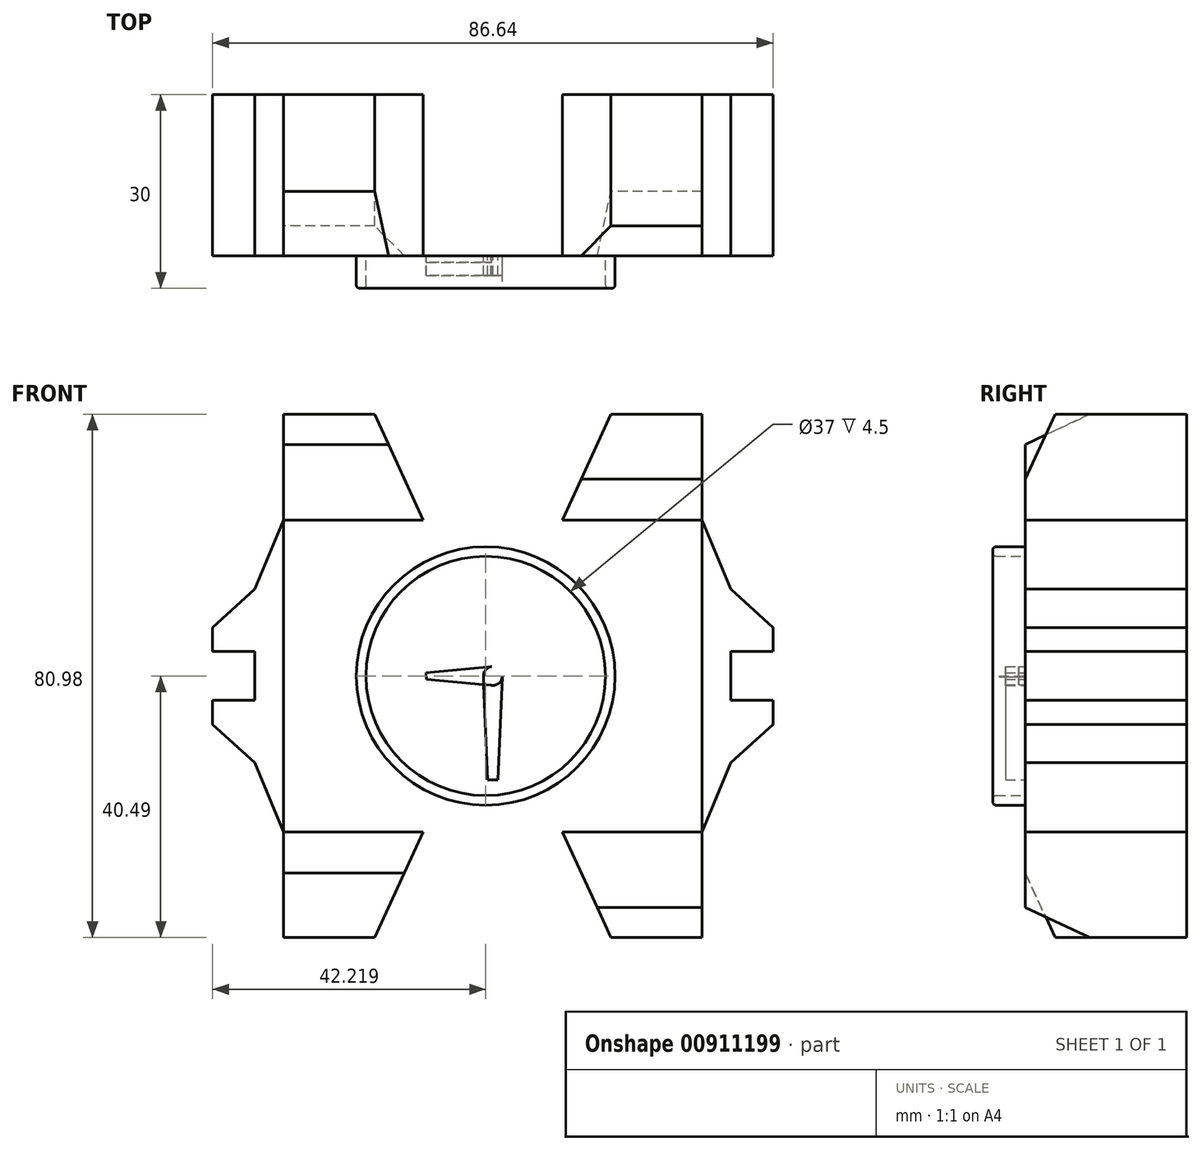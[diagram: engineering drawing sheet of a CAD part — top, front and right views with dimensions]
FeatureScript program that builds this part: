
annotation { "Feature Type Name" : "Feature", "Feature Type Description" : "" }
export const myFeature = defineFeature(function(context is Context, id is Id, definition is map)
    precondition{}
    {
        {
            var Q0;
            Q0=qCreatedBy(makeId("Front.planeOp"),FACE);
            var sketch = newSketch(context, id + "F0", { "sketchPlane" : qUnion([Q0])});
            skLineSegment(sketch, "E0.bottom", {"start": v(-32.34, 24.13) * mm, "end": v(32.34, 24.13) * mm});
            skLineSegment(sketch, "E0.top", {"start": v(-32.34, -24.13) * mm, "end": v(32.34, -24.13) * mm});
            skLineSegment(sketch, "E0.left", {"start": v(-32.34, 24.13) * mm, "end": v(-32.34, -24.13) * mm});
            skLineSegment(sketch, "E0.right", {"start": v(32.34, 24.13) * mm, "end": v(32.34, -24.13) * mm});
            skPoint(sketch, "E0.middle", {"position": v(0, 0) * mm});
            skLineSegment(sketch, "E1", {"start": v(32.34, 24.13) * mm, "end": v(36.78, 13.43) * mm});
            skLineSegment(sketch, "E2", {"start": v(36.78, 13.43) * mm, "end": v(43.32, 7.48) * mm});
            skLineSegment(sketch, "E3", {"start": v(43.32, 7.48) * mm, "end": v(43.32, 3.77) * mm});
            skLineSegment(sketch, "E4", {"start": v(43.32, 3.77) * mm, "end": v(36.78, 3.77) * mm});
            skLineSegment(sketch, "E5.MirrorCS", {"start": v(32.34, -24.13) * mm, "end": v(36.78, -13.43) * mm});
            skLineSegment(sketch, "E6.MirrorCS", {"start": v(36.78, -13.43) * mm, "end": v(43.32, -7.48) * mm});
            skLineSegment(sketch, "E7.MirrorCS", {"start": v(43.32, -3.77) * mm, "end": v(36.78, -3.77) * mm});
            skLineSegment(sketch, "E8.MirrorCS", {"start": v(43.32, -7.48) * mm, "end": v(43.32, -3.77) * mm});
            skLineSegment(sketch, "E9.MirrorCS", {"start": v(32.34, -24.13) * mm, "end": v(32.34, 24.13) * mm});
            skLineSegment(sketch, "E10.MirrorCS", {"start": v(-32.34, 24.13) * mm, "end": v(-36.78, 13.43) * mm});
            skLineSegment(sketch, "E11.MirrorCS", {"start": v(-36.78, -13.43) * mm, "end": v(-43.32, -7.48) * mm});
            skLineSegment(sketch, "E12.MirrorCS", {"start": v(-43.32, 7.48) * mm, "end": v(-43.32, 3.77) * mm});
            skLineSegment(sketch, "E13.MirrorCS", {"start": v(-43.32, -7.48) * mm, "end": v(-43.32, -3.77) * mm});
            skLineSegment(sketch, "E14.MirrorCS", {"start": v(-43.32, -3.77) * mm, "end": v(-36.78, -3.77) * mm});
            skLineSegment(sketch, "E15.MirrorCS", {"start": v(-32.34, -24.13) * mm, "end": v(-36.78, -13.43) * mm});
            skLineSegment(sketch, "E16.MirrorCS", {"start": v(-36.78, 13.43) * mm, "end": v(-43.32, 7.48) * mm});
            skLineSegment(sketch, "E17.MirrorCS", {"start": v(-43.32, 3.77) * mm, "end": v(-36.78, 3.77) * mm});
            skLineSegment(sketch, "E18.MirrorCS", {"start": v(-32.34, -24.13) * mm, "end": v(-32.34, 24.13) * mm});
            skLineSegment(sketch, "E19", {"start": v(36.78, -3.77) * mm, "end": v(36.78, 3.77) * mm});
            skLineSegment(sketch, "E20", {"start": v(-36.78, -3.77) * mm, "end": v(-36.78, 3.77) * mm});
            skLineSegment(sketch, "E21", {"start": v(-32.34, 24.13) * mm, "end": v(-32.34, 40.49) * mm});
            skLineSegment(sketch, "E22", {"start": v(-32.34, 40.49) * mm, "end": v(-18.27, 40.49) * mm});
            skLineSegment(sketch, "E23", {"start": v(-18.27, 40.49) * mm, "end": v(-10.77, 24.13) * mm});
            skLineSegment(sketch, "E24.MirrorCS", {"start": v(32.34, 40.49) * mm, "end": v(18.27, 40.49) * mm});
            skLineSegment(sketch, "E25.MirrorCS", {"start": v(32.34, 24.13) * mm, "end": v(32.34, 40.49) * mm});
            skLineSegment(sketch, "E26.MirrorCS", {"start": v(18.27, 40.49) * mm, "end": v(10.77, 24.13) * mm});
            skLineSegment(sketch, "E27.MirrorCS", {"start": v(32.34, -24.13) * mm, "end": v(32.34, -40.49) * mm});
            skLineSegment(sketch, "E28.MirrorCS", {"start": v(-32.34, -40.49) * mm, "end": v(-18.27, -40.49) * mm});
            skLineSegment(sketch, "E29.MirrorCS", {"start": v(18.27, -40.49) * mm, "end": v(10.77, -24.13) * mm});
            skLineSegment(sketch, "E30.MirrorCS", {"start": v(-32.34, -24.13) * mm, "end": v(-32.34, -40.49) * mm});
            skLineSegment(sketch, "E31.MirrorCS", {"start": v(-18.27, -40.49) * mm, "end": v(-10.77, -24.13) * mm});
            skLineSegment(sketch, "E32.MirrorCS", {"start": v(32.34, -40.49) * mm, "end": v(18.27, -40.49) * mm});
            skSolve(sketch);
        }
        {
            var Q0;
            {var subQ3=sQuery(id+"F0.wireOp",EDGE,"E9.MirrorCS");Q0=makeQuery(id+"F0.imprint","IMPRINT",FACE,{"disambiguationData":[TD([[makeQuery(id+"F0.imprint","IMPRINT",EDGE,{"derivedFrom":subQ3}),1.0]])]});}
            var Q1;
            {var subQ0=sQuery(id+"F0.wireOp",EDGE,"E30.MirrorCS");Q1=makeQuery(id+"F0.imprint","IMPRINT",FACE,{"disambiguationData":[TD([[makeQuery(id+"F0.imprint","IMPRINT",EDGE,{"derivedFrom":subQ0}),1.0]])]});}
            var Q2;
            Q2=makeQuery(id+"F0.imprint","IMPRINT",FACE,{"disambiguationData":[TD([[makeQuery(id+"F0.imprint","IMPRINT",EDGE,{"derivedFrom":sQuery(id+"F0.wireOp",EDGE,"E32.MirrorCS")}),-1.0]])]});
            var Q3;
            Q3=makeQuery(id+"F0.imprint","IMPRINT",FACE,{"disambiguationData":[TD([[makeQuery(id+"F0.imprint","IMPRINT",EDGE,{"derivedFrom":sQuery(id+"F0.wireOp",EDGE,"E6.MirrorCS")}),1.0]])]});
            var Q4;
            Q4=makeQuery(id+"F0.imprint","IMPRINT",FACE,{"disambiguationData":[TD([[makeQuery(id+"F0.imprint","IMPRINT",EDGE,{"derivedFrom":sQuery(id+"F0.wireOp",EDGE,"E24.MirrorCS")}),1.0]])]});
            var Q5;
            {var subQ2=sQuery(id+"F0.wireOp",EDGE,"E23");Q5=makeQuery(id+"F0.imprint","IMPRINT",FACE,{"disambiguationData":[TD([[makeQuery(id+"F0.imprint","IMPRINT",EDGE,{"derivedFrom":subQ2}),-1.0]])]});}
            var Q6;
            Q6=makeQuery(id+"F0.imprint","IMPRINT",FACE,{"disambiguationData":[TD([[makeQuery(id+"F0.imprint","IMPRINT",EDGE,{"derivedFrom":sQuery(id+"F0.wireOp",EDGE,"E13.MirrorCS")}),-1.0]])]});
            extrude(context, id + "F1", {"entities" : qUnion([Q0, Q1, Q2, Q3, Q4, Q5, Q6]), "depth" : 25 * mm, "offsetDistance" : 25 * mm});
        }
        {
            var Q0;
            Q0=makeQuery(id+"F1.opExtrude","CAP_EDGE",EDGE,{"disambiguationData":[OSD([sQuery(id+"F0.wireOp",EDGE,"E28.MirrorCS")])],"isStart":false});
            var Q1;
            Q1=makeQuery(id+"F1.opExtrude","CAP_EDGE",EDGE,{"disambiguationData":[OSD([sQuery(id+"F0.wireOp",EDGE,"E32.MirrorCS")])],"isStart":false});
            var Q2;
            Q2=makeQuery(id+"F1.opExtrude","CAP_EDGE",EDGE,{"disambiguationData":[OSD([sQuery(id+"F0.wireOp",EDGE,"E24.MirrorCS")])],"isStart":false});
            var Q3;
            Q3=makeQuery(id+"F1.opExtrude","CAP_EDGE",EDGE,{"disambiguationData":[OSD([sQuery(id+"F0.wireOp",EDGE,"E22")])],"isStart":false});
            chamfer(context, id + "F2", {"entities" : qUnion([Q0, Q1, Q2, Q3]), "chamferType" : ChamferType.OFFSET_ANGLE, "width" : 10 * mm, "oppositeDirection" : false, "angle" : 25 * degree, "tangentPropagation" : true});
        }
        {
            var Q0;
            Q0=makeQuery(id+"F1.opExtrude","CAP_FACE",FACE,{"disambiguationData":[OSD([sQuery(id+"F0.wireOp",EDGE,"E0.bottom"),sQuery(id+"F0.wireOp",EDGE,"E0.top"),sQuery(id+"F0.wireOp",EDGE,"E6.MirrorCS"),sQuery(id+"F0.wireOp",EDGE,"E3"),sQuery(id+"F0.wireOp",EDGE,"E5.MirrorCS"),sQuery(id+"F0.wireOp",EDGE,"E8.MirrorCS"),sQuery(id+"F0.wireOp",EDGE,"E4"),sQuery(id+"F0.wireOp",EDGE,"E2"),sQuery(id+"F0.wireOp",EDGE,"E1"),sQuery(id+"F0.wireOp",EDGE,"E7.MirrorCS"),sQuery(id+"F0.wireOp",EDGE,"E13.MirrorCS"),sQuery(id+"F0.wireOp",EDGE,"E14.MirrorCS"),sQuery(id+"F0.wireOp",EDGE,"E12.MirrorCS"),sQuery(id+"F0.wireOp",EDGE,"E17.MirrorCS"),sQuery(id+"F0.wireOp",EDGE,"E10.MirrorCS"),sQuery(id+"F0.wireOp",EDGE,"E16.MirrorCS"),sQuery(id+"F0.wireOp",EDGE,"E15.MirrorCS"),sQuery(id+"F0.wireOp",EDGE,"E11.MirrorCS"),sQuery(id+"F0.wireOp",EDGE,"E19"),sQuery(id+"F0.wireOp",EDGE,"E20"),sQuery(id+"F0.wireOp",EDGE,"E23"),sQuery(id+"F0.wireOp",EDGE,"E21"),sQuery(id+"F0.wireOp",EDGE,"E22"),sQuery(id+"F0.wireOp",EDGE,"E24.MirrorCS"),sQuery(id+"F0.wireOp",EDGE,"E25.MirrorCS"),sQuery(id+"F0.wireOp",EDGE,"E26.MirrorCS"),sQuery(id+"F0.wireOp",EDGE,"E32.MirrorCS"),sQuery(id+"F0.wireOp",EDGE,"E29.MirrorCS"),sQuery(id+"F0.wireOp",EDGE,"E27.MirrorCS"),sQuery(id+"F0.wireOp",EDGE,"E30.MirrorCS"),sQuery(id+"F0.wireOp",EDGE,"E28.MirrorCS"),sQuery(id+"F0.wireOp",EDGE,"E31.MirrorCS")])],"isStart":false});
            var sketch = newSketch(context, id + "F3", { "sketchPlane" : qUnion([Q0])});
            skCircle(sketch, "E33", {"center": v(-1.1, 0) * mm, "radius": 20 * mm});
            skCircle(sketch, "E34", {"center": v(-1.1, 0) * mm, "radius": 18.5 * mm});
            skSolve(sketch);
        }
        {
            var Q0;
            Q0=makeQuery(id+"F3.imprint","IMPRINT",FACE,{"disambiguationData":[TD([[makeQuery(id+"F3.imprint","IMPRINT",EDGE,{"derivedFrom":sQuery(id+"F3.wireOp",EDGE,"E33")}),1.0]])]});
            extrude(context, id + "F4", {"entities" : qUnion([Q0]), "operationType" : NewBodyOperationType.ADD, "depth" : 5 * mm, "offsetDistance" : 25 * mm});
        }
        {
            var Q0;
            Q0=makeQuery(id+"F4.opExtrude","CAP_EDGE",EDGE,{"disambiguationData":[OSD([sQuery(id+"F3.wireOp",EDGE,"E33")])],"isStart":false});
            var Q1;
            Q1=makeQuery(id+"F4.opExtrude","CAP_EDGE",EDGE,{"disambiguationData":[OSD([sQuery(id+"F3.wireOp",EDGE,"E34")])],"isStart":false});
            fillet(context, id + "F5", {"entities" : qUnion([Q0, Q1]), "radius" : 0.5 * mm, "tangentPropagation" : true, "allowEdgeOverflow" : false});
        }
        {
            var Q0;
            Q0=makeQuery(id+"F4.boolean.opBoolean","SPLIT",FACE,{"disambiguationData":[TD([makeQuery(id+"F4.opExtrude","SWEPT_FACE",FACE,{"disambiguationData":[OSD([sQuery(id+"F3.wireOp",EDGE,"E34")])]})])],"derivedFrom":makeQuery(id+"F1.opExtrude","CAP_FACE",FACE,{"disambiguationData":[OSD([sQuery(id+"F0.wireOp",EDGE,"E0.bottom"),sQuery(id+"F0.wireOp",EDGE,"E0.top"),sQuery(id+"F0.wireOp",EDGE,"E6.MirrorCS"),sQuery(id+"F0.wireOp",EDGE,"E3"),sQuery(id+"F0.wireOp",EDGE,"E5.MirrorCS"),sQuery(id+"F0.wireOp",EDGE,"E8.MirrorCS"),sQuery(id+"F0.wireOp",EDGE,"E4"),sQuery(id+"F0.wireOp",EDGE,"E2"),sQuery(id+"F0.wireOp",EDGE,"E1"),sQuery(id+"F0.wireOp",EDGE,"E7.MirrorCS"),sQuery(id+"F0.wireOp",EDGE,"E13.MirrorCS"),sQuery(id+"F0.wireOp",EDGE,"E14.MirrorCS"),sQuery(id+"F0.wireOp",EDGE,"E12.MirrorCS"),sQuery(id+"F0.wireOp",EDGE,"E17.MirrorCS"),sQuery(id+"F0.wireOp",EDGE,"E10.MirrorCS"),sQuery(id+"F0.wireOp",EDGE,"E16.MirrorCS"),sQuery(id+"F0.wireOp",EDGE,"E15.MirrorCS"),sQuery(id+"F0.wireOp",EDGE,"E11.MirrorCS"),sQuery(id+"F0.wireOp",EDGE,"E19"),sQuery(id+"F0.wireOp",EDGE,"E20"),sQuery(id+"F0.wireOp",EDGE,"E23"),sQuery(id+"F0.wireOp",EDGE,"E21"),sQuery(id+"F0.wireOp",EDGE,"E22"),sQuery(id+"F0.wireOp",EDGE,"E24.MirrorCS"),sQuery(id+"F0.wireOp",EDGE,"E25.MirrorCS"),sQuery(id+"F0.wireOp",EDGE,"E26.MirrorCS"),sQuery(id+"F0.wireOp",EDGE,"E32.MirrorCS"),sQuery(id+"F0.wireOp",EDGE,"E29.MirrorCS"),sQuery(id+"F0.wireOp",EDGE,"E27.MirrorCS"),sQuery(id+"F0.wireOp",EDGE,"E30.MirrorCS"),sQuery(id+"F0.wireOp",EDGE,"E28.MirrorCS"),sQuery(id+"F0.wireOp",EDGE,"E31.MirrorCS")])],"isStart":false})});
            var sketch = newSketch(context, id + "F6", { "sketchPlane" : qUnion([Q0])});
            skCircle(sketch, "E35", {"center": v(0, 0) * mm, "radius": 1.46 * mm});
            skLineSegment(sketch, "E36", {"start": v(-1.46, 0) * mm, "end": v(-0.8, -16.1) * mm});
            skLineSegment(sketch, "E37", {"start": v(-0.8, -16.1) * mm, "end": v(0, -16.06) * mm});
            skLineSegment(sketch, "E38.MirrorCS", {"start": v(0.8, -16.1) * mm, "end": v(0, -16.06) * mm});
            skLineSegment(sketch, "E39.MirrorCS", {"start": v(1.46, 0) * mm, "end": v(0.8, -16.1) * mm});
            skLineSegment(sketch, "E40", {"start": v(0, -1.46) * mm, "end": v(-10.26, -0.5) * mm});
            skLineSegment(sketch, "E41", {"start": v(-10.26, -0.5) * mm, "end": v(-10.28, 0) * mm});
            skLineSegment(sketch, "E42", {"start": v(-10.28, 0) * mm, "end": v(-10.3, 0.5) * mm});
            skLineSegment(sketch, "E43", {"start": v(-10.3, 0.5) * mm, "end": v(0, 1.47) * mm});
            skSolve(sketch);
        }
        {
            var Q0;
            {var subQ0=sQuery(id+"F6.wireOp",EDGE,"E37");Q0=makeQuery(id+"F6.imprint","IMPRINT",FACE,{"disambiguationData":[TD([[makeQuery(id+"F6.imprint","IMPRINT",EDGE,{"derivedFrom":subQ0}),1.0]])]});}
            var Q1;
            {var subQ0=sQuery(id+"F6.wireOp",EDGE,"E36");var subQ1=sQuery(id+"F6.wireOp",EDGE,"E35");var subQ2=makeQuery(id+"F6.imprint","INTERSECT",VERTEX,{"disambiguationData":[OD(1.0)],"derivedFrom":[subQ1,subQ0]});Q1=makeQuery(id+"F6.imprint","IMPRINT",FACE,{"disambiguationData":[TD([[makeQuery(id+"F6.imprint","IMPRINT",EDGE,{"disambiguationData":[TD([[subQ2,-1.0]])],"derivedFrom":subQ1}),-1.0]])]});}
            extrude(context, id + "F7", {"entities" : qUnion([Q0, Q1]), "operationType" : NewBodyOperationType.ADD, "depth" : 3 * mm, "offsetDistance" : 25 * mm});
        }
        {
            var Q0;
            {var subQ1=sQuery(id+"F6.wireOp",EDGE,"E35");var subQ8=sQuery(id+"F6.wireOp",EDGE,"E39.MirrorCS");var subQ9=makeQuery(id+"F6.imprint","INTERSECT",VERTEX,{"disambiguationData":[OD(0.0)],"derivedFrom":[subQ1,subQ8]});Q0=makeQuery(id+"F6.imprint","IMPRINT",FACE,{"disambiguationData":[TD([[makeQuery(id+"F6.imprint","IMPRINT",EDGE,{"disambiguationData":[TD([[subQ9,-1.0]])],"derivedFrom":subQ1}),1.0]])]});}
            extrude(context, id + "F8", {"entities" : qUnion([Q0]), "operationType" : NewBodyOperationType.ADD, "depth" : 4 * mm, "offsetDistance" : 25 * mm});
        }
        {
            var Q0;
            {var subQ9=sQuery(id+"F6.wireOp",EDGE,"E41");Q0=makeQuery(id+"F6.imprint","IMPRINT",FACE,{"disambiguationData":[TD([[makeQuery(id+"F6.imprint","IMPRINT",EDGE,{"derivedFrom":subQ9}),-1.0]])]});}
            var Q1;
            {var subQ0=sQuery(id+"F6.wireOp",EDGE,"E36");var subQ1=sQuery(id+"F6.wireOp",EDGE,"E35");var subQ2=makeQuery(id+"F6.imprint","INTERSECT",VERTEX,{"disambiguationData":[OD(1.0)],"derivedFrom":[subQ1,subQ0]});Q1=makeQuery(id+"F6.imprint","IMPRINT",FACE,{"disambiguationData":[TD([[makeQuery(id+"F6.imprint","IMPRINT",EDGE,{"disambiguationData":[TD([[subQ2,-1.0]])],"derivedFrom":subQ1}),-1.0]])]});}
            extrude(context, id + "F9", {"entities" : qUnion([Q0, Q1]), "depth" : 1 * mm, "offsetDistance" : 25 * mm});
        }
    });
